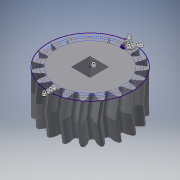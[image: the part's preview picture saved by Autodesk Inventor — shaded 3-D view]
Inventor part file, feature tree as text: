
AUTODESK INVENTOR PART (.ipt)
format: ipt  version: 2017 (Build 210142000, 142)  size: 714,752 bytes
history: native  units: mm
features: sketch x3, extrude x3, pattern_circular x2, helix x2, projected_geometry x1
ambient origin geometry x8: Origin, YZ Plane, XZ Plane, XY Plane, X Axis, Y Axis, Z Axis, Center Point
bodies: Solid1 (feature_tree)
feature tree (11):
  sketch  "Sketch1"  dims[d0=20.0mm d1=0.0mm]
  extrude  "Extrusion1"  TaperAngle=0.0deg  [1 undecoded]
  extrude  "Extrusion2"  Depth=190.0mm TaperAngle=360.0deg
  pattern_circular  "Circular Pattern1"  [2 undecoded]
  extrude  "Extrusion3"  Depth=190.0mm TaperAngle=360.0deg
  helix  "Coil1"  [1 undecoded]
  helix  "Coil2"  [1 undecoded]
  pattern_circular  "Circular Pattern2"  [2 undecoded]
  sketch  "Sketch2"  dims[d2=10.0mm d3=0.0mm d4=190.0mm d5=360.0deg]
  sketch  "Sketch3"  dims[d7=9.525mm d8=10.0mm d9=0.0mm d10=10.0mm d11=10.0mm d12=0.1mm d13=0.0mm d14=90.0deg d15=90.0deg d16=0.0mm d17=0.0mm d18=10.0mm d19=10.0mm d20=0.1mm d21=0.0mm d22=90.0deg d23=90.0deg d24=0.0mm d25=0.0mm d26=190.0mm d27=360.0deg]
  projected_geometry  "Projected Loop1"
note: 7 required parameter values undecoded (feature->parameter linkage not recoverable at this tier; creation-order binding heuristic only, values carry confidence <= 0.55)
